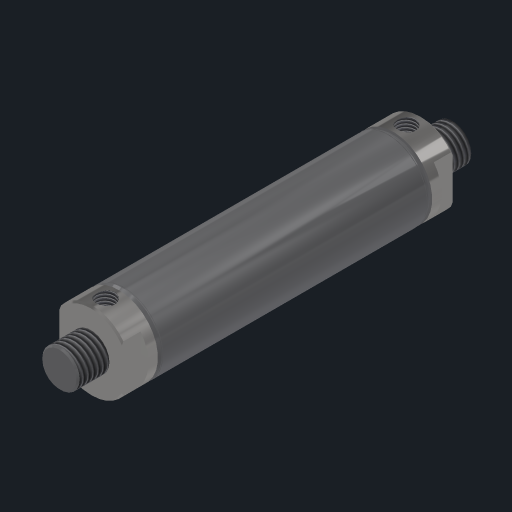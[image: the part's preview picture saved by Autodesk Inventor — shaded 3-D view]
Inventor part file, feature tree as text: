
AUTODESK INVENTOR PART (.ipt)
format: ipt  version: 2023 (Build 270158030, 158C)  size: 234,496 bytes
history: native  units: in
note: dims shown in document units (in); Inventor stores cm internally (conversion verified against a paired STEP export)
features: thread x4, mirror x1, imported_body x1
ambient origin geometry x8: Origin, YZ Plane, XZ Plane, XY Plane, X Axis, Y Axis, Z Axis, Center Point
bodies: Body1 (feature_tree)
feature tree (6):
  mirror  "Mirror1"
  imported_body  "Base1"
  thread  "Thread1"  [1 undecoded]
  thread  "Thread2"  [1 undecoded]
  thread  "Thread3"  [1 undecoded]
  thread  "Thread4"  [1 undecoded]
note: 4 required parameter values undecoded (feature->parameter linkage not recoverable at this tier; creation-order binding heuristic only, values carry confidence <= 0.55)
